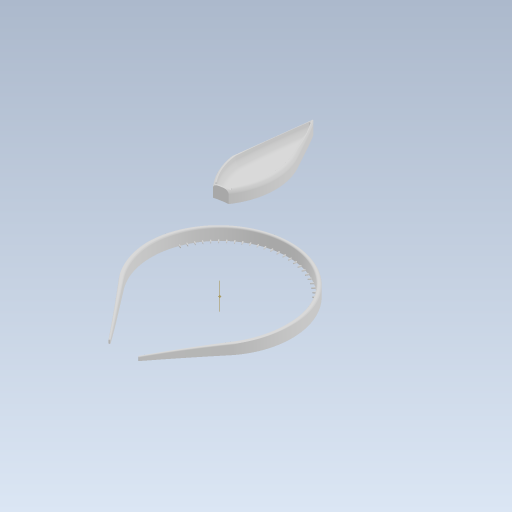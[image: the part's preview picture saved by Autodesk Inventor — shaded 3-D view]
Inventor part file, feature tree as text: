
AUTODESK INVENTOR PART (.ipt)
format: ipt  version: 2023 (Build 270158030, 158C)  size: 1,804,800 bytes
history: native  units: in
note: dims shown in document units (in); Inventor stores cm internally (conversion verified against a paired STEP export)
features: fillet x14, extrude x9, sketch x8, other x1, pattern_circular x1, chamfer x1, projected_geometry x1
ambient origin geometry x8: Origin, YZ Plane, XZ Plane, XY Plane, X Axis, Y Axis, Z Axis, Center Point
bodies: Solid1 (feature_tree), Solid2 (feature_tree)
feature tree (35):
  extrude  "Extrusion1"  TaperAngle=0.0deg  [1 undecoded]
  extrude  "Extrusion2"  Depth=2.2638in
  fillet  "Fillet2"  Radius=0.1181in
  other  "Work Axis1"
  pattern_circular  "Circular Pattern1"  [2 undecoded]
  extrude  "Extrusion3"  Depth=11.811in
  extrude  "Extrusion4"  Depth=0.889in
  fillet  "Fillet5"  Radius=3.1496in
  fillet  "Fillet6"  Radius=0.0394in
  fillet  "Fillet7"  Radius=0.0118in
  fillet  "Fillet8"  Radius=0.0427in
  fillet  "Fillet19"  Radius=59.0551in
  extrude  "Extrusion5"  Depth=59.0551in
  extrude  "Extrusion7"  Depth=0.3937in TaperAngle=0.0deg
  extrude  "Extrusion6"  Depth=0.1181in
  fillet  "Fillet20"  Radius=4.3307in
  fillet  "Fillet21"  Radius=25.1969in
  fillet  "Fillet22"  Radius=0.7087in
  fillet  "Fillet23"  Radius=4.3307in
  fillet  "Fillet24"  Radius=0.3937in
  fillet  "Fillet25"  [1 undecoded]
  fillet  "Fillet26"  Radius=0.0248in
  extrude  "Extrusion8"  Depth=0.0394in
  fillet  "Fillet27"  Radius=0.0394in
  extrude  "Extrusion9"  Depth=0.0236in
  chamfer  "Chamfer1"  Distance=0.3937in
  sketch  "Sketch2"  dims[d18=0.0in d19=0.0in]
  sketch  "Sketch5"  dims[d20=0.0in d23=2.2638in d25=0.1181in]
  sketch  "Sketch6"  dims[d26=0.1181in]
  sketch  "Sketch7"  dims[d27=0.1181in]
  sketch  "Sketch8"  dims[d30=0.3937in d31=0.0in]
  sketch  "Sketch9"  dims[d48=0.0433in d49=0.0in]
  sketch  "Sketch11"  dims[d50=0.0118in]
  sketch  "Sketch12"  dims[d57=0.0787in d58=0.0157in d59=0.7594in d60=2.1102in d61=11.811in d62=-0.962in d64=0.889in d65=3.1496in d68=0.0394in d69=0.0118in d70=0.0427in d71=59.0551in d72=59.0551in d73=0.3937in d74=0.0in d75=0.1181in d76=4.3307in d77=25.1969in d78=0.7087in d79=4.3307in d80=0.3937in d81=0.0in d82=0.0in d85=0.0248in d86=0.0394in d87=0.0394in d88=0.0236in d104=0.3937in d105=0.0in d107=0.315in d108=0.0in d121=0.0591in d122=0.0591in d123=1.378in d125=0.3346in d126=0.0in d130=2.3495in d131=2.2052in d132=2.0826in d133=1.4138in d134=2.5284in d135=1.4901in d136=2.1896in d137=2.5146in d138=2.7368in d139=1.4623in d140=0.488in d141=0.3104in d142=0.2859in d143=0.2088in d144=0.2171in d145=0.23in d147=0.2362in d148=0.0787in d149=0.0787in d150=0.0394in d153=0.0394in d154=0.1181in d155=0.0787in d156=0.0787in d158=23.622in d159=1.9685in d161=7.8078in d162=2.3622in d163=0.7874in d164=0.9817in d165=0.0in d166=0.0in d167=0.0787in d168=0.1969in d169=0.1969in d170=0.1181in d171=0.0197in d172=0.0079in d173=0.0394in d174=0.0197in d175=0.0197in d182=0.0984in d183=0.0394in d184=0.0984in d185=0.0394in d186=0.0591in d187=0.0394in d188=0.0197in d189=0.076in d190=0.0in d191=0.0in d192=0.0079in d193=0.0197in d194=0.0787in d195=45.0deg d196=0.0in d197=0.0in]
  projected_geometry  "Projected Loop1"
note: 4 required parameter values undecoded (feature->parameter linkage not recoverable at this tier; creation-order binding heuristic only, values carry confidence <= 0.55)
